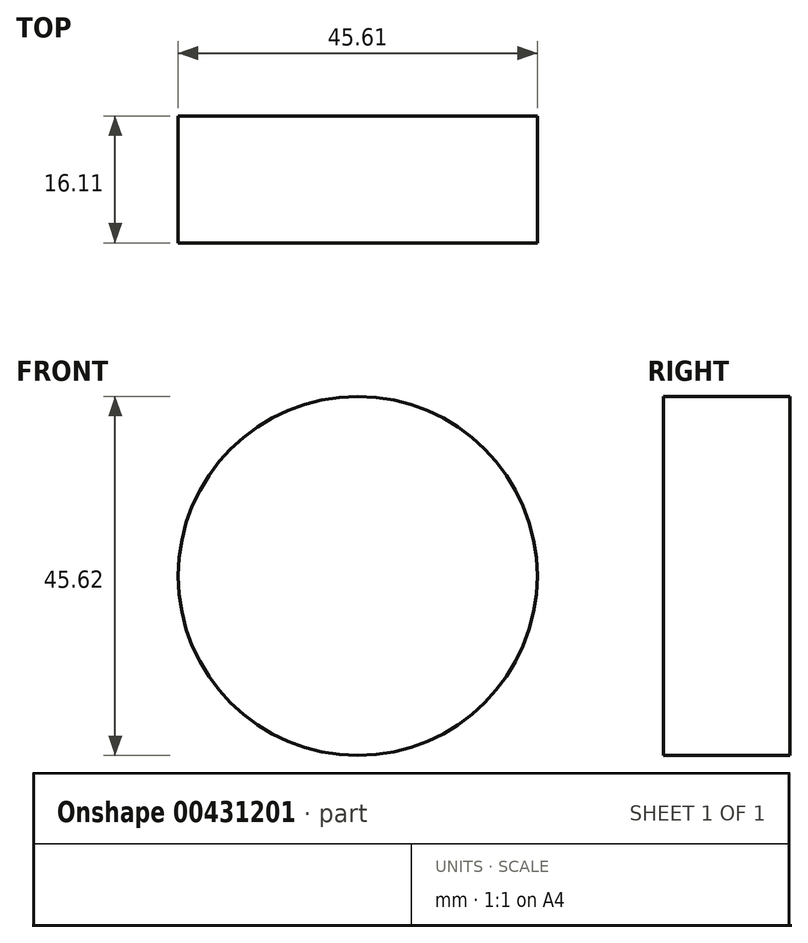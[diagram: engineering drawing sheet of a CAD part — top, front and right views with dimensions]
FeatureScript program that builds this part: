
annotation { "Feature Type Name" : "Feature", "Feature Type Description" : "" }
export const myFeature = defineFeature(function(context is Context, id is Id, definition is map)
    precondition{}
    {
        {
            var Q0;
            Q0=qCreatedBy(makeId("Front.planeOp"),FACE);
            var sketch = newSketch(context, id + "F0", { "sketchPlane" : qUnion([Q0])});
            skCircle(sketch, "E0", {"center": v(36.05, 21.82) * mm, "radius": 22.8 * mm});
            skPoint(sketch, "E0.first.point", {"position": v(47.46, 41.57) * mm});
            skPoint(sketch, "E0.second.point", {"position": v(14.79, 13.58) * mm});
            skPoint(sketch, "E0.third.point", {"position": v(29.42, 0) * mm});
            skSolve(sketch);
        }
        {
            var Q0;
            Q0=makeQuery(id+"F0.imprint","IMPRINT",FACE,{"disambiguationData":[TD([[makeQuery(id+"F0.imprint","IMPRINT",EDGE,{"derivedFrom":sQuery(id+"F0.wireOp",EDGE,"E0")}),1.0]])]});
            extrude(context, id + "F1", {"entities" : qUnion([Q0]), "depth" : 16.1 * mm});
        }
    });
